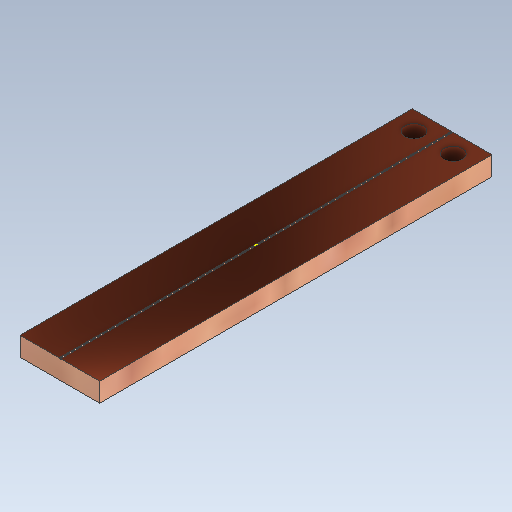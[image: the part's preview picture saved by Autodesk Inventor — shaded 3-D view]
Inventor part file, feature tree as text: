
AUTODESK INVENTOR PART (.ipt)
format: ipt  version: 2021 (Build 250183000, 183)  size: 132,608 bytes
history: native  units: in
note: dims shown in document units (in); Inventor stores cm internally (conversion verified against a paired STEP export)
features: sketch x4, other x3
ambient origin geometry x8: Origin, YZ Plane, XZ Plane, XY Plane, X Axis, Y Axis, Z Axis, Center Point
bodies: Solid1 (feature_tree)
feature tree (7):
  other  "Leads+ChannelForSingleHeater.ipt"
  other  "Solid1::Leads+ChannelForSingleHeater.ipt"
  other  "TaggingFeature1"
  sketch  "Sketch1"  dims[d0=0.3937in]
  sketch  "Sketch2"  dims[d1=0.12in]
  sketch  "Sketch3"
  sketch  "Sketch4"
